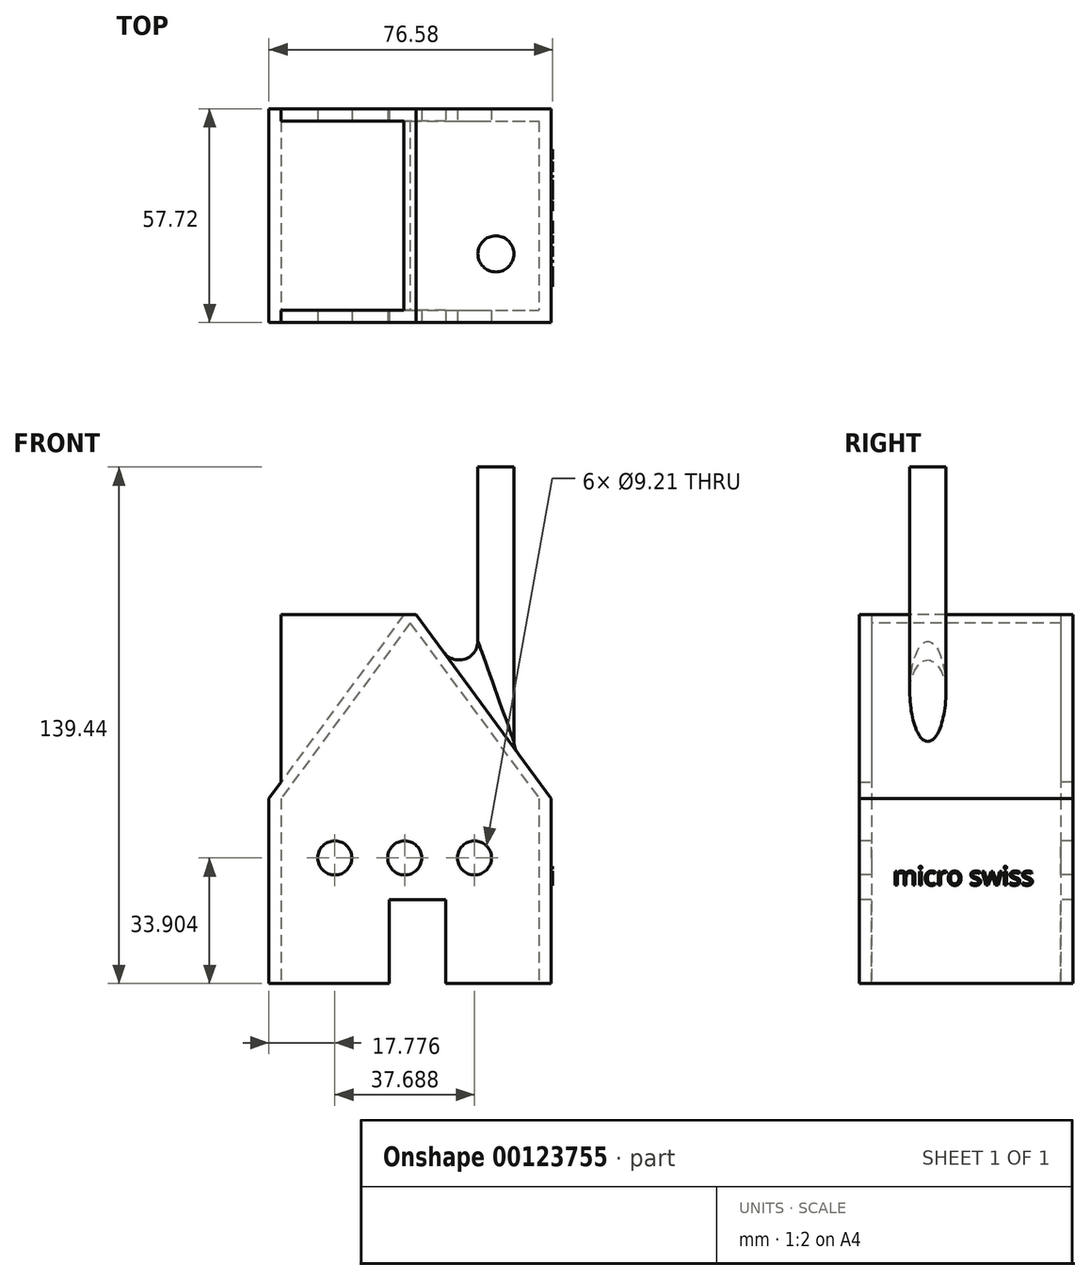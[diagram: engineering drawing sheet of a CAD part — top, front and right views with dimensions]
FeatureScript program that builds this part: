
annotation { "Feature Type Name" : "Feature", "Feature Type Description" : "" }
export const myFeature = defineFeature(function(context is Context, id is Id, definition is map)
    precondition{}
    {
        {
            var Q0;
            Q0=qCreatedBy(makeId("Top.planeOp"),FACE);
            var sketch = newSketch(context, id + "F0", { "sketchPlane" : qUnion([Q0])});
            skLineSegment(sketch, "E0.bottom", {"start": v(-38.1, 28.86) * mm, "end": v(38.1, 28.86) * mm});
            skLineSegment(sketch, "E0.top", {"start": v(-38.1, -28.86) * mm, "end": v(38.1, -28.86) * mm});
            skLineSegment(sketch, "E0.left", {"start": v(-38.1, 28.86) * mm, "end": v(-38.1, -28.86) * mm});
            skLineSegment(sketch, "E0.right", {"start": v(38.1, 28.86) * mm, "end": v(38.1, -28.86) * mm});
            skLineSegment(sketch, "E1", {"start": v(-38.1, 28.86) * mm, "end": v(38.1, -28.86) * mm, "construction": true});
            skLineSegment(sketch, "E2.0", {"start": v(-34.8, 25.56) * mm, "end": v(34.8, 25.56) * mm});
            skLineSegment(sketch, "E2.1", {"start": v(-34.8, 25.56) * mm, "end": v(-34.8, -25.56) * mm});
            skLineSegment(sketch, "E2.2", {"start": v(-34.8, -25.56) * mm, "end": v(34.8, -25.56) * mm});
            skLineSegment(sketch, "E2.3", {"start": v(34.8, 25.56) * mm, "end": v(34.8, -25.56) * mm});
            skSolve(sketch);
        }
        {
            var Q0;
            Q0=makeQuery(id+"F0.imprint","IMPRINT",FACE,{"disambiguationData":[TD([[makeQuery(id+"F0.imprint","IMPRINT",EDGE,{"derivedFrom":sQuery(id+"F0.wireOp",EDGE,"E0.bottom")}),-1.0]])]});
            extrude(context, id + "F1", {"entities" : qUnion([Q0]), "depth" : 49.95 * mm});
        }
        {
            var Q0;
            Q0=makeQuery(id+"F1.opExtrude","SWEPT_FACE",FACE,{"disambiguationData":[OSD([sQuery(id+"F0.wireOp",EDGE,"E0.top")])]});
            var sketch = newSketch(context, id + "F2", { "sketchPlane" : qUnion([Q0])});
            skCircle(sketch, "E3", {"center": v(-20.32, 33.9) * mm, "radius": 4.6 * mm});
            skCircle(sketch, "E4.1.0.0", {"center": v(-1.48, 33.9) * mm, "radius": 4.6 * mm});
            skCircle(sketch, "E4.2.0.0", {"center": v(17.36, 33.9) * mm, "radius": 4.6 * mm});
            skLineSegment(sketch, "E4.direction1", {"start": v(-20.32, 33.9) * mm, "end": v(-1.48, 33.9) * mm, "construction": true});
            skLineSegment(sketch, "E5.bottom", {"start": v(-5.62, 22.56) * mm, "end": v(9.62, 22.56) * mm});
            skLineSegment(sketch, "E5.top", {"start": v(-5.62, 0) * mm, "end": v(9.62, 0) * mm});
            skLineSegment(sketch, "E5.left", {"start": v(-5.62, 22.56) * mm, "end": v(-5.62, 0) * mm});
            skLineSegment(sketch, "E5.right", {"start": v(9.62, 22.56) * mm, "end": v(9.62, 0) * mm});
            skSolve(sketch);
        }
        {
            var Q0;
            Q0=makeQuery(id+"F2.imprint","IMPRINT",FACE,{"disambiguationData":[TD([[makeQuery(id+"F2.imprint","IMPRINT",EDGE,{"derivedFrom":sQuery(id+"F2.wireOp",EDGE,"E5.bottom")}),-1.0]])]});
            var Q1;
            Q1=makeQuery(id+"F2.imprint","IMPRINT",FACE,{"disambiguationData":[TD([[makeQuery(id+"F2.imprint","IMPRINT",EDGE,{"derivedFrom":sQuery(id+"F2.wireOp",EDGE,"E4.1.0.0")}),1.0]])]});
            var Q2;
            Q2=makeQuery(id+"F2.imprint","IMPRINT",FACE,{"disambiguationData":[TD([[makeQuery(id+"F2.imprint","IMPRINT",EDGE,{"derivedFrom":sQuery(id+"F2.wireOp",EDGE,"E3")}),1.0]])]});
            var Q3;
            Q3=makeQuery(id+"F2.imprint","IMPRINT",FACE,{"disambiguationData":[TD([[makeQuery(id+"F2.imprint","IMPRINT",EDGE,{"derivedFrom":sQuery(id+"F2.wireOp",EDGE,"E4.2.0.0")}),1.0]])]});
            extrude(context, id + "F3", {"entities" : qUnion([Q0, Q1, Q2, Q3]), "operationType" : NewBodyOperationType.REMOVE, "oppositeDirection" : true, "depth" : 60.6 * mm});
        }
        {
            var Q0;
            Q0=makeQuery(id+"F1.opExtrude","SWEPT_FACE",FACE,{"disambiguationData":[OSD([sQuery(id+"F0.wireOp",EDGE,"E0.right")])]});
            var sketch = newSketch(context, id + "F4", { "sketchPlane" : qUnion([Q0])});
            skText(sketch, "E6", { "text": "micro swiss", "fontName": "OpenSans-Regular.ttf"});
            const initialGuessF4  = {"E6": [-0.01977, 0.02653, 1, 0, 0.00507]};
            skSetInitialGuess(sketch, initialGuessF4);
            skSolve(sketch);
        }
        {
            var Q0;
            Q0 = qSketchRegion(id + "F4", true);
            extrude(context, id + "F5", {"entities" : qUnion([Q0]), "operationType" : NewBodyOperationType.ADD, "depth" : 0.38 * mm});
        }
        {
            var Q0;
            Q0=makeQuery(id+"F1.opExtrude","CAP_FACE",FACE,{"disambiguationData":[OSD([sQuery(id+"F0.wireOp",EDGE,"E0.bottom"),sQuery(id+"F0.wireOp",EDGE,"E0.top"),sQuery(id+"F0.wireOp",EDGE,"E0.left"),sQuery(id+"F0.wireOp",EDGE,"E0.right"),sQuery(id+"F0.wireOp",EDGE,"E2.0"),sQuery(id+"F0.wireOp",EDGE,"E2.1"),sQuery(id+"F0.wireOp",EDGE,"E2.2"),sQuery(id+"F0.wireOp",EDGE,"E2.3")])],"isStart":false});
            var sketch = newSketch(context, id + "F6", { "sketchPlane" : qUnion([Q0])});
            skLineSegment(sketch, "E7", {"start": v(-34.8, 25.56) * mm, "end": v(-34.8, 28.86) * mm});
            skLineSegment(sketch, "E8", {"start": v(34.8, 25.56) * mm, "end": v(34.8, 28.86) * mm});
            skLineSegment(sketch, "E9", {"start": v(34.8, -25.56) * mm, "end": v(34.8, -28.86) * mm});
            skLineSegment(sketch, "E10", {"start": v(-34.8, -25.56) * mm, "end": v(-34.8, -28.86) * mm});
            skSolve(sketch);
        }
        {
            var Q0;
            {var subQ0=sQuery(id+"F6.wireOp",EDGE,"E9");Q0=makeQuery(id+"F6.imprint","IMPRINT",FACE,{"disambiguationData":[TD([[makeQuery(id+"F6.imprint","IMPRINT",EDGE,{"derivedFrom":subQ0}),-1.0]])]});}
            var Q1;
            {var subQ0=sQuery(id+"F6.wireOp",EDGE,"E7");Q1=makeQuery(id+"F6.imprint","IMPRINT",FACE,{"disambiguationData":[TD([[makeQuery(id+"F6.imprint","IMPRINT",EDGE,{"derivedFrom":subQ0}),-1.0]])]});}
            extrude(context, id + "F7", {"entities" : qUnion([Q0, Q1]), "operationType" : NewBodyOperationType.ADD, "depth" : 49.6 * mm});
        }
        {
            var Q0;
            {var subQ0=sQuery(id+"F0.wireOp",EDGE,"E0.top");Q0=makeQuery(id+"F7.boolean.opBoolean","MERGE",FACE,{"derivedFrom":[makeQuery(id+"F1.opExtrude","SWEPT_FACE",FACE,{"disambiguationData":[OSD([subQ0])]}),makeQuery(id+"F7.opExtrude","SWEPT_FACE",FACE,{"disambiguationData":[OSD([subQ0])]})]});}
            var sketch = newSketch(context, id + "F8", { "sketchPlane" : qUnion([Q0])});
            skLineSegment(sketch, "E11.0", {"start": v(-38.1, 49.95) * mm, "end": v(-34.8, 49.95) * mm});
            skLineSegment(sketch, "E12.0", {"start": v(34.8, 49.95) * mm, "end": v(38.1, 49.95) * mm});
            skLineSegment(sketch, "E13", {"start": v(-36.45, 49.95) * mm, "end": v(0, 99.55) * mm, "construction": true});
            skLineSegment(sketch, "E14", {"start": v(0, 99.55) * mm, "end": v(36.45, 49.95) * mm, "construction": true});
            skLineSegment(sketch, "E15", {"start": v(-38.1, 49.95) * mm, "end": v(-1.65, 99.55) * mm});
            skLineSegment(sketch, "E16.MirrorCS", {"start": v(-34.8, 49.95) * mm, "end": v(0, 97.3) * mm});
            skLineSegment(sketch, "E17", {"start": v(0, 99.55) * mm, "end": v(0, 59.74) * mm, "construction": true});
            skLineSegment(sketch, "E18.MirrorCS", {"start": v(34.8, 49.95) * mm, "end": v(0, 97.3) * mm});
            skLineSegment(sketch, "E19.MirrorCS", {"start": v(38.1, 49.95) * mm, "end": v(1.65, 99.55) * mm});
            skLineSegment(sketch, "E20.0", {"start": v(-1.65, 99.55) * mm, "end": v(1.65, 99.55) * mm});
            skPoint(sketch, "E21.orphan", {"position": v(0.74, 102.8) * mm});
            skPoint(sketch, "E22.orphan", {"position": v(-0.74, 102.8) * mm});
            skPoint(sketch, "E23.orphan", {"position": v(-2.88, 101.22) * mm});
            skPoint(sketch, "E24.orphan", {"position": v(2.88, 101.22) * mm});
            skPoint(sketch, "E25.orphan", {"position": v(34.8, 99.55) * mm});
            skPoint(sketch, "E26.orphan", {"position": v(-34.8, 99.55) * mm});
            skPoint(sketch, "E27.orphan", {"position": v(35.96, 48.37) * mm});
            skPoint(sketch, "E28.orphan", {"position": v(-35.96, 48.37) * mm});
            skSolve(sketch);
        }
        {
            var Q0;
            {var subQ0=sQuery(id+"F8.wireOp",EDGE,"E12.0");Q0=makeQuery(id+"F8.imprint","IMPRINT",FACE,{"disambiguationData":[TD([[makeQuery(id+"F8.imprint","IMPRINT",EDGE,{"derivedFrom":subQ0}),1.0]])]});}
            var Q1;
            {var subQ7=sQuery(id+"F8.wireOp",EDGE,"E18.MirrorCS");Q1=makeQuery(id+"F8.imprint","IMPRINT",FACE,{"disambiguationData":[TD([[makeQuery(id+"F8.imprint","IMPRINT",EDGE,{"derivedFrom":subQ7}),-1.0]])]});}
            var Q2;
            {var subQ0=sQuery(id+"F8.wireOp",EDGE,"E11.0");Q2=makeQuery(id+"F8.imprint","IMPRINT",FACE,{"disambiguationData":[TD([[makeQuery(id+"F8.imprint","IMPRINT",EDGE,{"derivedFrom":subQ0}),1.0]])]});}
            var Q3;
            {var subQ0=sQuery(id+"F0.wireOp",EDGE,"E0.bottom");Q3=makeQuery(id+"F7.boolean.opBoolean","MERGE",FACE,{"derivedFrom":[makeQuery(id+"F1.opExtrude","SWEPT_FACE",FACE,{"disambiguationData":[OSD([subQ0])]}),makeQuery(id+"F7.opExtrude","SWEPT_FACE",FACE,{"disambiguationData":[OSD([subQ0])]})]});}
            extrude(context, id + "F9", {"entities" : qUnion([Q0, Q1, Q2]), "operationType" : NewBodyOperationType.ADD, "endBound" : BoundingType.UP_TO_SURFACE, "oppositeDirection" : true, "endBoundEntityFace" : qUnion([Q3]), "depth" : 25.4 * mm});
        }
        {
            var Q0;
            Q0=makeQuery(id+"F9.opExtrude","SWEPT_FACE",FACE,{"disambiguationData":[OSD([sQuery(id+"F8.wireOp",EDGE,"E19.MirrorCS")])]});
            var sketch = newSketch(context, id + "F10", { "sketchPlane" : qUnion([Q0])});
            skLineSegment(sketch, "E29.bottom", {"start": v(-51.84, 96.8) * mm, "end": v(50.28, 96.8) * mm});
            skLineSegment(sketch, "E29.top", {"start": v(-51.84, 7.2) * mm, "end": v(50.28, 7.2) * mm});
            skLineSegment(sketch, "E29.left", {"start": v(-51.84, 96.8) * mm, "end": v(-51.84, 7.2) * mm});
            skLineSegment(sketch, "E29.right", {"start": v(50.28, 96.8) * mm, "end": v(50.28, 7.2) * mm});
            skSolve(sketch);
        }
        {
            var Q0;
            Q0=makeQuery(id+"F10.imprint","IMPRINT",FACE,{"disambiguationData":[TD([[makeQuery(id+"F10.imprint","IMPRINT",EDGE,{"derivedFrom":sQuery(id+"F10.wireOp",EDGE,"E29.bottom")}),-1.0]])]});
            var Q1;
            {var subQ0=sQuery(id+"F8.wireOp",EDGE,"E19.MirrorCS");Q1=makeQuery(id+"F10.imprint","IMPRINT",FACE,{"disambiguationData":[TD([[makeQuery(id+"F10.imprint","IMPRINT",EDGE,{"derivedFrom":makeQuery(id+"F9.opExtrude","CAP_EDGE",EDGE,{"disambiguationData":[OSD([subQ0])],"isStart":true})}),-1.0]])]});}
            extrude(context, id + "F11", {"entities" : qUnion([Q0, Q1]), "operationType" : NewBodyOperationType.REMOVE, "depth" : 48.6 * mm});
        }
        {
            var Q0;
            Q0=makeQuery(id+"F9.boolean.opBoolean","MERGE",FACE,{"derivedFrom":[makeQuery(id+"F7.opExtrude","CAP_FACE",FACE,{"disambiguationData":[OSD([sQuery(id+"F0.wireOp",EDGE,"E0.bottom"),sQuery(id+"F0.wireOp",EDGE,"E2.0"),sQuery(id+"F6.wireOp",EDGE,"E7"),sQuery(id+"F6.wireOp",EDGE,"E8")])],"isStart":false}),makeQuery(id+"F7.opExtrude","CAP_FACE",FACE,{"disambiguationData":[OSD([sQuery(id+"F0.wireOp",EDGE,"E0.top"),sQuery(id+"F0.wireOp",EDGE,"E2.2"),sQuery(id+"F6.wireOp",EDGE,"E9"),sQuery(id+"F6.wireOp",EDGE,"E10")])],"isStart":false}),makeQuery(id+"F9.opExtrude","SWEPT_FACE",FACE,{"disambiguationData":[OSD([sQuery(id+"F8.wireOp",EDGE,"E20.0")])]})]});
            var sketch = newSketch(context, id + "F12", { "sketchPlane" : qUnion([Q0])});
            skCircle(sketch, "E30", {"center": v(23.14, -10.33) * mm, "radius": 4.87 * mm});
            skSolve(sketch);
        }
        {
            var Q0;
            Q0=makeQuery(id+"F12.imprint","IMPRINT",FACE,{"disambiguationData":[TD([[makeQuery(id+"F12.imprint","IMPRINT",EDGE,{"derivedFrom":sQuery(id+"F12.wireOp",EDGE,"E30")}),1.0]])]});
            extrude(context, id + "F13", {"entities" : qUnion([Q0]), "operationType" : NewBodyOperationType.ADD, "endBound" : BoundingType.SYMMETRIC, "depth" : 79.78 * mm});
        }
        {
            var Q0;
            Q0=makeQuery(id+"F9.opExtrude","SWEPT_FACE",FACE,{"disambiguationData":[OSD([sQuery(id+"F8.wireOp",EDGE,"E18.MirrorCS")])]});
            var sketch = newSketch(context, id + "F14", { "sketchPlane" : qUnion([Q0])});
            skCircle(sketch, "E31", {"center": v(10.8, 41.6) * mm, "radius": 13.14 * mm});
            skSolve(sketch);
        }
        {
            var Q0;
            Q0 = qSketchRegion(id + "F14", true);
            extrude(context, id + "F15", {"entities" : qUnion([Q0]), "operationType" : NewBodyOperationType.REMOVE, "depth" : 25.4 * mm});
        }
        {
            var Q0;
            Q0=makeQuery(id+"F13.boolean.opBoolean","INTERSECT",EDGE,{"derivedFrom":[makeQuery(id+"F11.boolean.opBoolean","MERGE",FACE,{"derivedFrom":[makeQuery(id+"F9.opExtrude","SWEPT_FACE",FACE,{"disambiguationData":[OSD([sQuery(id+"F8.wireOp",EDGE,"E19.MirrorCS")])]}),makeQuery(id+"F11.opExtrude","CAP_FACE",FACE,{"disambiguationData":[OSD([sQuery(id+"F10.wireOp",EDGE,"E29.bottom"),sQuery(id+"F10.wireOp",EDGE,"E29.top"),sQuery(id+"F10.wireOp",EDGE,"E29.left"),sQuery(id+"F10.wireOp",EDGE,"E29.right")])],"isStart":true})]}),makeQuery(id+"F13.opExtrude","SWEPT_FACE",FACE,{"disambiguationData":[OSD([sQuery(id+"F12.wireOp",EDGE,"E30")])]})]});
            fillet(context, id + "F16", {"entities" : qUnion([Q0]), "radius" : 5.08 * mm, "tangentPropagation" : true, "allowEdgeOverflow" : false});
        }
    });
